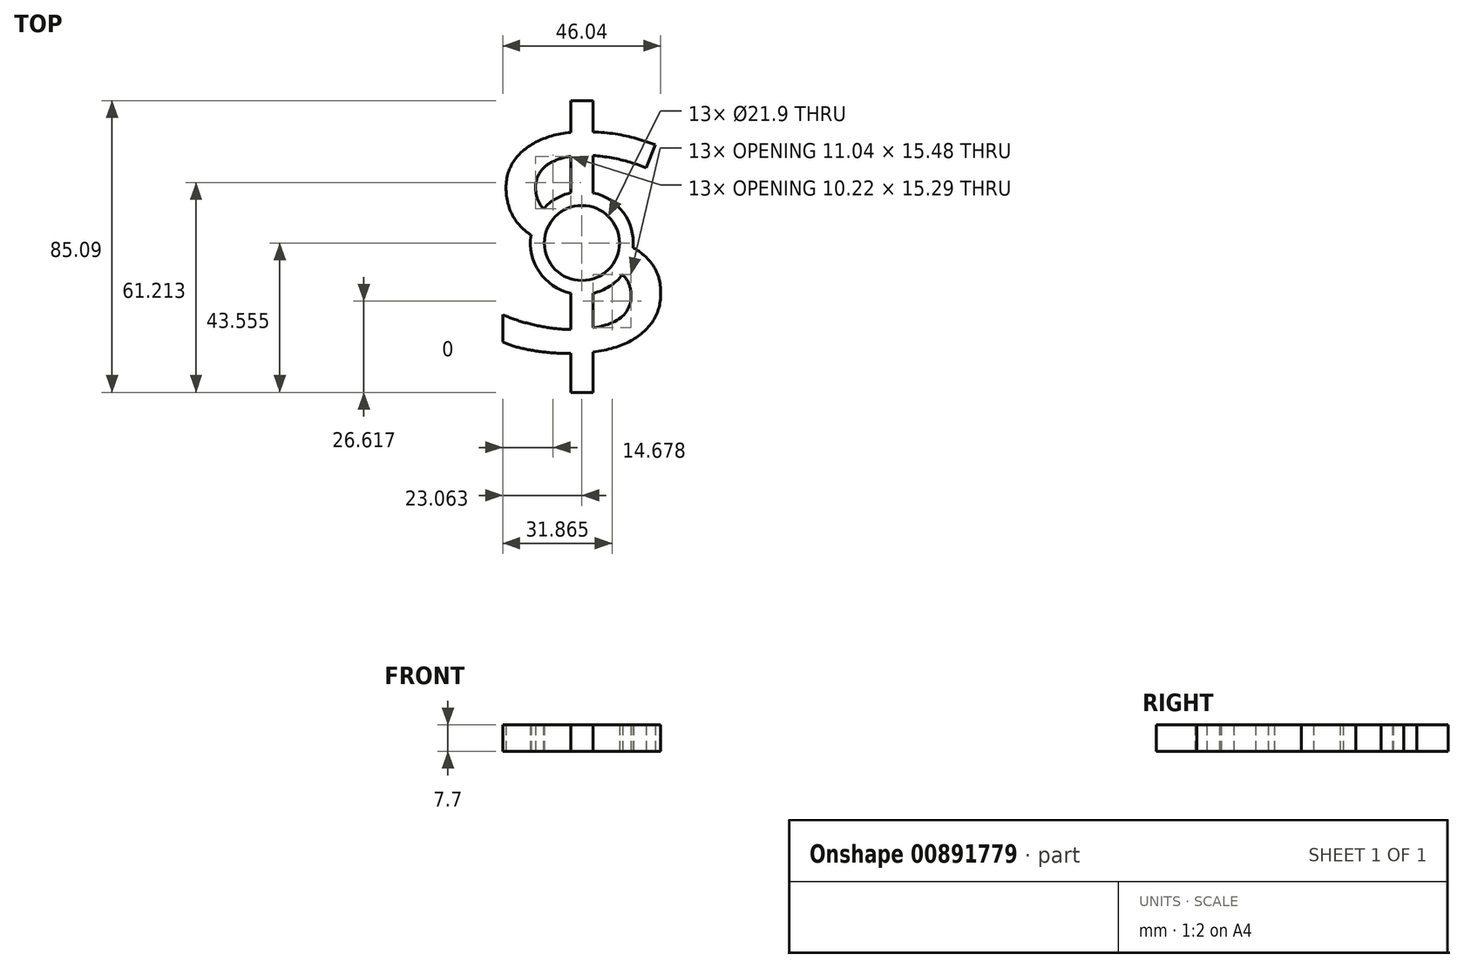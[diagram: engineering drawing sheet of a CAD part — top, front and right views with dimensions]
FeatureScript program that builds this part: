
annotation { "Feature Type Name" : "Feature", "Feature Type Description" : "" }
export const myFeature = defineFeature(function(context is Context, id is Id, definition is map)
    precondition{}
    {
        {
            var Q0;
            Q0=qCreatedBy(makeId("Top.planeOp"),FACE);
            var sketch = newSketch(context, id + "F0", { "sketchPlane" : qUnion([Q0])});
            skText(sketch, "E0", { "text": "$", "fontName": "OpenSans-Regular.ttf"});
            skCircle(sketch, "E1", {"center": v(7.15, -2.18) * mm, "radius": 15 * mm});
            skCircle(sketch, "E2", {"center": v(7.15, -2.18) * mm, "radius": 10.95 * mm});
            const initialGuessF0  = {"E0": [-0.02257, -0.03968, 1, 0, 0.075]};
            skSetInitialGuess(sketch, initialGuessF0);
            skSolve(sketch);
        }
        {
            var Q0;
            Q0=makeQuery(id+"F0.imprint","IMPRINT",FACE,{"disambiguationData":[TD([[makeQuery(id+"F0.imprint","IMPRINT",EDGE,{"derivedFrom":sQuery(id+"F0.wireOp",EDGE,"E0.sketch_text.stroke-0")}),-1.0]])]});
            var Q1;
            {var subQ8=sQuery(id+"F0.wireOp",EDGE,"E0.sketch_text.stroke-12");Q1=makeQuery(id+"F0.imprint","IMPRINT",FACE,{"disambiguationData":[TD([[makeQuery(id+"F0.imprint","IMPRINT",EDGE,{"derivedFrom":subQ8}),-1.0]])]});}
            var Q2;
            {var subQ0=sQuery(id+"F0.wireOp",EDGE,"E1");var subQ1=sQuery(id+"F0.wireOp",EDGE,"E0.sketch_text.stroke-10");var subQ2=makeQuery(id+"F0.imprint","INTERSECT",VERTEX,{"derivedFrom":[subQ1,subQ0]});Q2=makeQuery(id+"F0.imprint","IMPRINT",FACE,{"disambiguationData":[TD([[makeQuery(id+"F0.imprint","IMPRINT",EDGE,{"disambiguationData":[TD([[subQ2,-1.0]])],"derivedFrom":subQ1}),-1.0]])]});}
            var Q3;
            {var subQ0=sQuery(id+"F0.wireOp",EDGE,"E1");var subQ1=sQuery(id+"F0.wireOp",EDGE,"E0.sketch_text.stroke-21");var subQ2=makeQuery(id+"F0.imprint","INTERSECT",VERTEX,{"derivedFrom":[subQ1,subQ0]});Q3=makeQuery(id+"F0.imprint","IMPRINT",FACE,{"disambiguationData":[TD([[makeQuery(id+"F0.imprint","IMPRINT",EDGE,{"disambiguationData":[TD([[subQ2,-1.0]])],"derivedFrom":subQ1}),-1.0]])]});}
            var Q4;
            {var subQ0=sQuery(id+"F0.wireOp",EDGE,"E1");var subQ1=sQuery(id+"F0.wireOp",EDGE,"E0.sketch_text.stroke-22");var subQ2=makeQuery(id+"F0.imprint","INTERSECT",VERTEX,{"derivedFrom":[subQ1,subQ0]});Q4=makeQuery(id+"F0.imprint","IMPRINT",FACE,{"disambiguationData":[TD([[makeQuery(id+"F0.imprint","IMPRINT",EDGE,{"disambiguationData":[TD([[subQ2,1.0]])],"derivedFrom":subQ1}),-1.0]])]});}
            var Q5;
            {var subQ0=sQuery(id+"F0.wireOp",EDGE,"E1");var subQ1=sQuery(id+"F0.wireOp",EDGE,"E0.sketch_text.stroke-11");var subQ2=makeQuery(id+"F0.imprint","INTERSECT",VERTEX,{"derivedFrom":[subQ1,subQ0]});Q5=makeQuery(id+"F0.imprint","IMPRINT",FACE,{"disambiguationData":[TD([[makeQuery(id+"F0.imprint","IMPRINT",EDGE,{"disambiguationData":[TD([[subQ2,1.0]])],"derivedFrom":subQ1}),-1.0]])]});}
            var Q6;
            {var subQ0=sQuery(id+"F0.wireOp",EDGE,"E1");var subQ1=sQuery(id+"F0.wireOp",EDGE,"E0.sketch_text.stroke-10");var subQ2=makeQuery(id+"F0.imprint","INTERSECT",VERTEX,{"derivedFrom":[subQ1,subQ0]});Q6=makeQuery(id+"F0.imprint","IMPRINT",FACE,{"disambiguationData":[TD([[makeQuery(id+"F0.imprint","IMPRINT",EDGE,{"disambiguationData":[TD([[subQ2,-1.0]])],"derivedFrom":subQ1}),1.0]])]});}
            var Q7;
            {var subQ0=sQuery(id+"F0.wireOp",EDGE,"E1");var subQ1=sQuery(id+"F0.wireOp",EDGE,"E0.sketch_text.stroke-26");var subQ2=makeQuery(id+"F0.imprint","INTERSECT",VERTEX,{"derivedFrom":[subQ1,subQ0]});Q7=makeQuery(id+"F0.imprint","IMPRINT",FACE,{"disambiguationData":[TD([[makeQuery(id+"F0.imprint","IMPRINT",EDGE,{"disambiguationData":[TD([[subQ2,-1.0]])],"derivedFrom":subQ1}),1.0]])]});}
            var Q8;
            {var subQ0=sQuery(id+"F0.wireOp",EDGE,"E1");var subQ1=sQuery(id+"F0.wireOp",EDGE,"E0.sketch_text.stroke-21");var subQ2=makeQuery(id+"F0.imprint","INTERSECT",VERTEX,{"derivedFrom":[subQ1,subQ0]});Q8=makeQuery(id+"F0.imprint","IMPRINT",FACE,{"disambiguationData":[TD([[makeQuery(id+"F0.imprint","IMPRINT",EDGE,{"disambiguationData":[TD([[subQ2,-1.0]])],"derivedFrom":subQ1}),1.0]])]});}
            var Q9;
            {var subQ0=sQuery(id+"F0.wireOp",EDGE,"E1");var subQ1=sQuery(id+"F0.wireOp",EDGE,"E0.sketch_text.stroke-30");var subQ2=makeQuery(id+"F0.imprint","INTERSECT",VERTEX,{"derivedFrom":[subQ1,subQ0]});Q9=makeQuery(id+"F0.imprint","IMPRINT",FACE,{"disambiguationData":[TD([[makeQuery(id+"F0.imprint","IMPRINT",EDGE,{"disambiguationData":[TD([[subQ2,-1.0]])],"derivedFrom":subQ1}),1.0]])]});}
            extrude(context, id + "F1", {"entities" : qUnion([Q0, Q1, Q2, Q3, Q4, Q5, Q6, Q7, Q8, Q9]), "depth" : 7.7 * mm, "offsetDistance" : 25 * mm});
        }
    });
